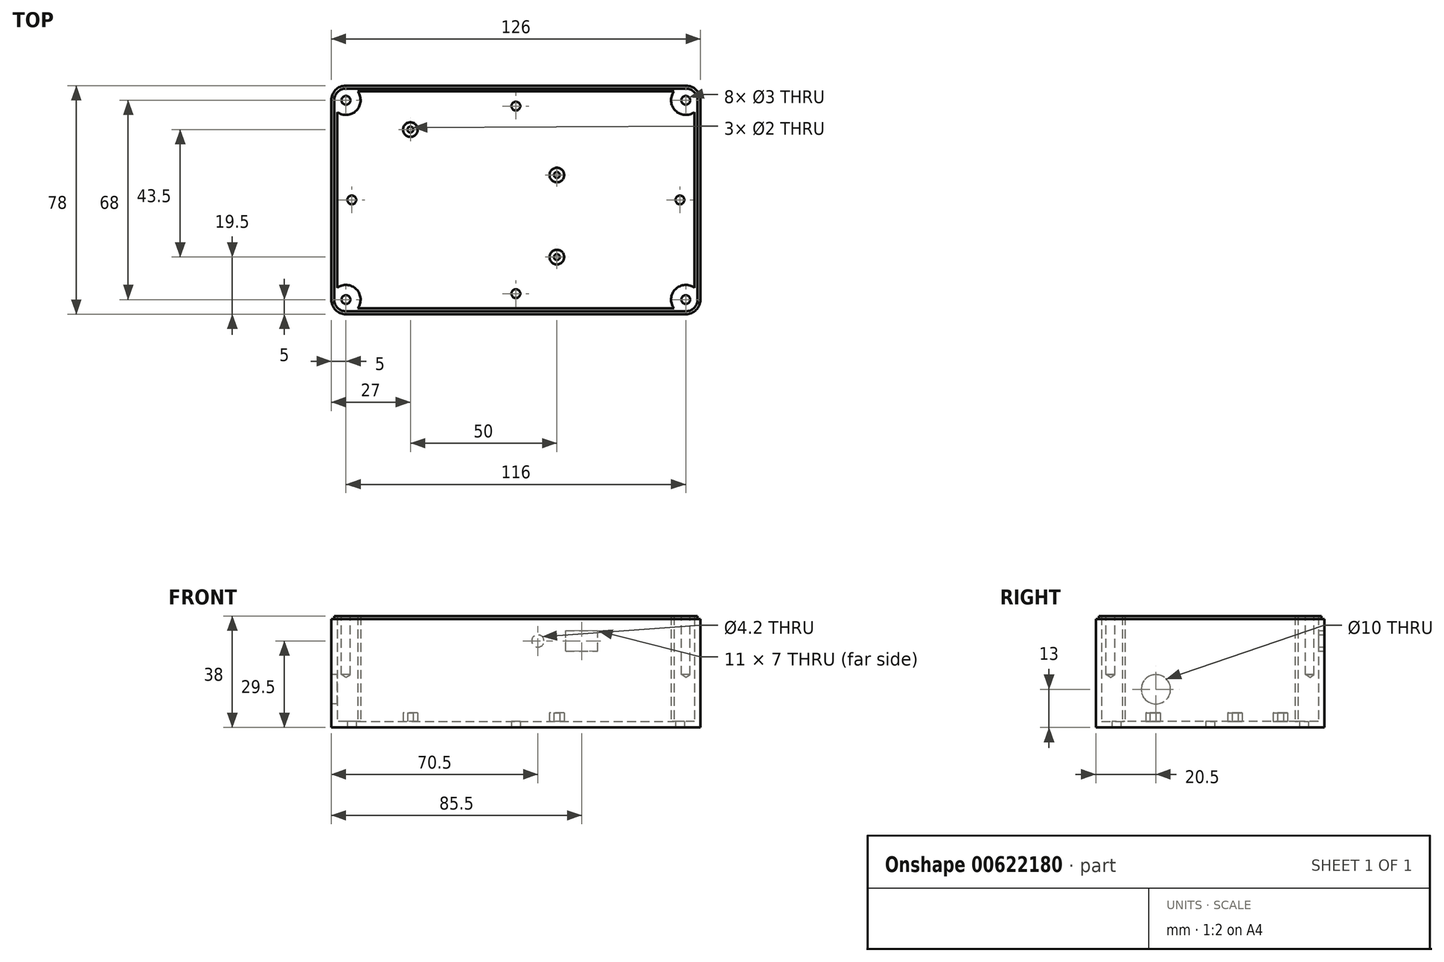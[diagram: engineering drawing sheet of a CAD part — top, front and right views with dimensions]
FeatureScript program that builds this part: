
annotation { "Feature Type Name" : "Feature", "Feature Type Description" : "" }
export const myFeature = defineFeature(function(context is Context, id is Id, definition is map)
    precondition{}
    {
        {
            var Q0;
            Q0=qCreatedBy(makeId("Top.planeOp"),FACE);
            var sketch = newSketch(context, id + "F0", { "sketchPlane" : qUnion([Q0])});
            skLineSegment(sketch, "E0.bottom", {"start": v(51, 27) * mm, "end": v(-51, 27) * mm});
            skLineSegment(sketch, "E0.top", {"start": v(51, -27) * mm, "end": v(-51, -27) * mm});
            skLineSegment(sketch, "E0.left", {"start": v(51, 27) * mm, "end": v(51, -27) * mm});
            skLineSegment(sketch, "E0.right", {"start": v(-51, 27) * mm, "end": v(-51, -27) * mm});
            skPoint(sketch, "E0.middle", {"position": v(0, 0) * mm});
            skPoint(sketch, "E1", {"position": v(-36, 24) * mm});
            skCircle(sketch, "E2", {"center": v(-36, 24) * mm, "radius": 2.5 * mm});
            skLineSegment(sketch, "E3.bottom", {"start": v(-56, 37) * mm, "end": v(56, 37) * mm});
            skLineSegment(sketch, "E3.top", {"start": v(-56, -37) * mm, "end": v(56, -37) * mm});
            skLineSegment(sketch, "E3.left", {"start": v(-61, 32) * mm, "end": v(-61, -32) * mm});
            skLineSegment(sketch, "E3.right", {"start": v(61, 32) * mm, "end": v(61, -32) * mm});
            skPoint(sketch, "E4", {"position": v(14, -19.5) * mm});
            skPoint(sketch, "E5", {"position": v(14, 8.5) * mm});
            skCircle(sketch, "E6", {"center": v(14, 8.5) * mm, "radius": 2.5 * mm});
            skCircle(sketch, "E7", {"center": v(14, -19.5) * mm, "radius": 2.5 * mm});
            skLineSegment(sketch, "E8.bottom", {"start": v(58, 39) * mm, "end": v(-58, 39) * mm});
            skLineSegment(sketch, "E8.top", {"start": v(58, -39) * mm, "end": v(-58, -39) * mm});
            skLineSegment(sketch, "E8.left", {"start": v(63, 34) * mm, "end": v(63, -34) * mm});
            skLineSegment(sketch, "E8.right", {"start": v(-63, 34) * mm, "end": v(-63, -34) * mm});
            skPoint(sketch, "E9.visualSharp", {"position": v(-63, 39) * mm});
            skArc(sketch, "E9.filletArc", {"start": v(-58, 39) * mm, "mid": v(-61.54, 37.54) * mm, "end": v(-63, 34) * mm});
            skPoint(sketch, "E10.visualSharp", {"position": v(63, 39) * mm});
            skArc(sketch, "E10.filletArc", {"start": v(63, 34) * mm, "mid": v(61.54, 37.54) * mm, "end": v(58, 39) * mm});
            skPoint(sketch, "E11.visualSharp", {"position": v(61, 37) * mm});
            skArc(sketch, "E11.filletArc", {"start": v(61, 32) * mm, "mid": v(59.54, 35.54) * mm, "end": v(56, 37) * mm});
            skPoint(sketch, "E12.visualSharp", {"position": v(63, -39) * mm});
            skArc(sketch, "E12.filletArc", {"start": v(58, -39) * mm, "mid": v(61.54, -37.54) * mm, "end": v(63, -34) * mm});
            skPoint(sketch, "E13.visualSharp", {"position": v(61, -37) * mm});
            skArc(sketch, "E13.filletArc", {"start": v(56, -37) * mm, "mid": v(59.54, -35.54) * mm, "end": v(61, -32) * mm});
            skPoint(sketch, "E14.visualSharp", {"position": v(-63, -39) * mm});
            skArc(sketch, "E14.filletArc", {"start": v(-63, -34) * mm, "mid": v(-61.54, -37.54) * mm, "end": v(-58, -39) * mm});
            skPoint(sketch, "E15.visualSharp", {"position": v(-61, -37) * mm});
            skArc(sketch, "E15.filletArc", {"start": v(-61, -32) * mm, "mid": v(-59.54, -35.54) * mm, "end": v(-56, -37) * mm});
            skPoint(sketch, "E16.visualSharp", {"position": v(-61, 37) * mm});
            skArc(sketch, "E16.filletArc", {"start": v(-56, 37) * mm, "mid": v(-59.54, 35.54) * mm, "end": v(-61, 32) * mm});
            skArc(sketch, "E17", {"start": v(-63, 34) * mm, "mid": v(-54.46, 30.46) * mm, "end": v(-58, 39) * mm});
            skArc(sketch, "E18", {"start": v(-58, -39) * mm, "mid": v(-54.46, -30.46) * mm, "end": v(-63, -34) * mm});
            skArc(sketch, "E19", {"start": v(63, -34) * mm, "mid": v(54.46, -30.46) * mm, "end": v(58, -39) * mm});
            skArc(sketch, "E20", {"start": v(58, 39) * mm, "mid": v(54.46, 30.46) * mm, "end": v(63, 34) * mm});
            skPoint(sketch, "E21", {"position": v(0, 32) * mm});
            skPoint(sketch, "E21.positionSnap0", {"position": v(0, 37) * mm});
            skPoint(sketch, "E22", {"position": v(0, -32) * mm});
            skPoint(sketch, "E22.positionSnap0", {"position": v(0, -37) * mm});
            skPoint(sketch, "E23", {"position": v(56, 0) * mm});
            skPoint(sketch, "E23.positionSnap0", {"position": v(61, 0) * mm});
            skPoint(sketch, "E24", {"position": v(-56, 0) * mm});
            skPoint(sketch, "E24.positionSnap0", {"position": v(-61, 0) * mm});
            skSolve(sketch);
        }
        {
            var Q0;
            Q0=makeQuery(id+"F0.imprint","IMPRINT",FACE,{"disambiguationData":[TD([[makeQuery(id+"F0.imprint","IMPRINT",EDGE,{"derivedFrom":sQuery(id+"F0.wireOp",EDGE,"E0.bottom")}),-1.0]])]});
            var Q1;
            Q1=makeQuery(id+"F0.imprint","IMPRINT",FACE,{"disambiguationData":[TD([[makeQuery(id+"F0.imprint","IMPRINT",EDGE,{"derivedFrom":sQuery(id+"F0.wireOp",EDGE,"E0.bottom")}),1.0]])]});
            extrude(context, id + "F1", {"entities" : qUnion([Q0, Q1]), "depth" : 2 * mm, "offsetDistance" : 25 * mm});
        }
        {
            var Q0;
            Q0=makeQuery(id+"F0.imprint","IMPRINT",FACE,{"disambiguationData":[TD([[makeQuery(id+"F0.imprint","IMPRINT",EDGE,{"derivedFrom":sQuery(id+"F0.wireOp",EDGE,"E2")}),1.0]])]});
            var Q1;
            Q1=makeQuery(id+"F0.imprint","IMPRINT",FACE,{"disambiguationData":[TD([[makeQuery(id+"F0.imprint","IMPRINT",EDGE,{"derivedFrom":sQuery(id+"F0.wireOp",EDGE,"E6")}),1.0]])]});
            var Q2;
            Q2=makeQuery(id+"F0.imprint","IMPRINT",FACE,{"disambiguationData":[TD([[makeQuery(id+"F0.imprint","IMPRINT",EDGE,{"derivedFrom":sQuery(id+"F0.wireOp",EDGE,"E7")}),1.0]])]});
            extrude(context, id + "F2", {"entities" : qUnion([Q0, Q1, Q2]), "operationType" : NewBodyOperationType.ADD, "depth" : 5 * mm, "offsetDistance" : 25 * mm});
        }
        {
            var Q0;
            {var subQ0=sQuery(id+"F0.wireOp",EDGE,"E9.filletArc");Q0=makeQuery(id+"F0.imprint","IMPRINT",FACE,{"disambiguationData":[TD([[makeQuery(id+"F0.imprint","IMPRINT",EDGE,{"derivedFrom":subQ0}),1.0]])]});}
            var Q1;
            {var subQ4=sQuery(id+"F0.wireOp",EDGE,"E10.filletArc");Q1=makeQuery(id+"F0.imprint","IMPRINT",FACE,{"disambiguationData":[TD([[makeQuery(id+"F0.imprint","IMPRINT",EDGE,{"derivedFrom":subQ4}),1.0]])]});}
            var Q2;
            {var subQ0=sQuery(id+"F0.wireOp",EDGE,"E11.filletArc");Q2=makeQuery(id+"F0.imprint","IMPRINT",FACE,{"disambiguationData":[TD([[makeQuery(id+"F0.imprint","IMPRINT",EDGE,{"derivedFrom":subQ0}),1.0]])]});}
            var Q3;
            {var subQ0=sQuery(id+"F0.wireOp",EDGE,"E16.filletArc");Q3=makeQuery(id+"F0.imprint","IMPRINT",FACE,{"disambiguationData":[TD([[makeQuery(id+"F0.imprint","IMPRINT",EDGE,{"derivedFrom":subQ0}),1.0]])]});}
            var Q4;
            {var subQ5=sQuery(id+"F0.wireOp",EDGE,"E8.right");Q4=makeQuery(id+"F0.imprint","IMPRINT",FACE,{"disambiguationData":[TD([[makeQuery(id+"F0.imprint","IMPRINT",EDGE,{"derivedFrom":subQ5}),1.0]])]});}
            var Q5;
            {var subQ5=sQuery(id+"F0.wireOp",EDGE,"E8.bottom");Q5=makeQuery(id+"F0.imprint","IMPRINT",FACE,{"disambiguationData":[TD([[makeQuery(id+"F0.imprint","IMPRINT",EDGE,{"derivedFrom":subQ5}),1.0]])]});}
            var Q6;
            {var subQ5=sQuery(id+"F0.wireOp",EDGE,"E8.left");Q6=makeQuery(id+"F0.imprint","IMPRINT",FACE,{"disambiguationData":[TD([[makeQuery(id+"F0.imprint","IMPRINT",EDGE,{"derivedFrom":subQ5}),-1.0]])]});}
            var Q7;
            {var subQ0=sQuery(id+"F0.wireOp",EDGE,"E13.filletArc");Q7=makeQuery(id+"F0.imprint","IMPRINT",FACE,{"disambiguationData":[TD([[makeQuery(id+"F0.imprint","IMPRINT",EDGE,{"derivedFrom":subQ0}),1.0]])]});}
            var Q8;
            {var subQ0=sQuery(id+"F0.wireOp",EDGE,"E15.filletArc");Q8=makeQuery(id+"F0.imprint","IMPRINT",FACE,{"disambiguationData":[TD([[makeQuery(id+"F0.imprint","IMPRINT",EDGE,{"derivedFrom":subQ0}),1.0]])]});}
            var Q9;
            {var subQ1=sQuery(id+"F0.wireOp",EDGE,"E14.filletArc");Q9=makeQuery(id+"F0.imprint","IMPRINT",FACE,{"disambiguationData":[TD([[makeQuery(id+"F0.imprint","IMPRINT",EDGE,{"derivedFrom":subQ1}),1.0]])]});}
            var Q10;
            {var subQ5=sQuery(id+"F0.wireOp",EDGE,"E8.top");Q10=makeQuery(id+"F0.imprint","IMPRINT",FACE,{"disambiguationData":[TD([[makeQuery(id+"F0.imprint","IMPRINT",EDGE,{"derivedFrom":subQ5}),-1.0]])]});}
            var Q11;
            {var subQ4=sQuery(id+"F0.wireOp",EDGE,"E12.filletArc");Q11=makeQuery(id+"F0.imprint","IMPRINT",FACE,{"disambiguationData":[TD([[makeQuery(id+"F0.imprint","IMPRINT",EDGE,{"derivedFrom":subQ4}),1.0]])]});}
            extrude(context, id + "F3", {"entities" : qUnion([Q0, Q1, Q2, Q3, Q4, Q5, Q6, Q7, Q8, Q9, Q10, Q11]), "operationType" : NewBodyOperationType.ADD, "depth" : 38 * mm, "offsetDistance" : 25 * mm});
        }
        {
            var Q0;
            Q0=sQuery(id+"F0.wireOp",VERTEX,"E23");
            var Q1;
            Q1=sQuery(id+"F0.wireOp",VERTEX,"E24");
            var Q2;
            Q2=sQuery(id+"F0.wireOp",VERTEX,"E22");
            var Q3;
            Q3=sQuery(id+"F0.wireOp",VERTEX,"E21");
            var Q4;
            Q4=makeQuery(id+"F1.opExtrude","SWEPT_BODY",BODY,{"disambiguationData":[OSD([sQuery(id+"F0.wireOp",EDGE,"E2"),sQuery(id+"F0.wireOp",EDGE,"E3.bottom"),sQuery(id+"F0.wireOp",EDGE,"E3.top"),sQuery(id+"F0.wireOp",EDGE,"E3.left"),sQuery(id+"F0.wireOp",EDGE,"E3.right"),sQuery(id+"F0.wireOp",EDGE,"E6"),sQuery(id+"F0.wireOp",EDGE,"E7"),sQuery(id+"F0.wireOp",EDGE,"E17"),sQuery(id+"F0.wireOp",EDGE,"E18"),sQuery(id+"F0.wireOp",EDGE,"E19"),sQuery(id+"F0.wireOp",EDGE,"E20")])]});
            hole(context, id + "F4", {"style" : HoleStyle.SIMPLE, "endStyle" : HoleEndStyle.BLIND, "oppositeDirection" : true, "standardTappedOrClearance" : lookupTablePath({ "standard" : "ISO", "size" : "3", "type" : "Drilled" }), "standardBlindInLast" : lookupTablePath({ "standard" : "ISO", "size" : "3", "type" : "Drilled" }), "holeDiameter" : 3 * mm, "majorDiameter" : 5 * mm, "holeDepth" : 5 * mm, "isTappedThrough" : true, "tappedDepth" : 12 * mm, "tapClearance" : 3, "locations" : qUnion([Q0, Q1, Q2, Q3]), "scope" : qUnion([Q4])});
        }
        {
            var Q0;
            Q0=makeQuery(id+"F3.opExtrude","CAP_FACE",FACE,{"disambiguationData":[OSD([sQuery(id+"F0.wireOp",EDGE,"E3.bottom"),sQuery(id+"F0.wireOp",EDGE,"E3.top"),sQuery(id+"F0.wireOp",EDGE,"E3.left"),sQuery(id+"F0.wireOp",EDGE,"E3.right"),sQuery(id+"F0.wireOp",EDGE,"E8.bottom"),sQuery(id+"F0.wireOp",EDGE,"E8.top"),sQuery(id+"F0.wireOp",EDGE,"E8.left"),sQuery(id+"F0.wireOp",EDGE,"E8.right"),sQuery(id+"F0.wireOp",EDGE,"E9.filletArc"),sQuery(id+"F0.wireOp",EDGE,"E10.filletArc"),sQuery(id+"F0.wireOp",EDGE,"E12.filletArc"),sQuery(id+"F0.wireOp",EDGE,"E14.filletArc"),sQuery(id+"F0.wireOp",EDGE,"E17"),sQuery(id+"F0.wireOp",EDGE,"E18"),sQuery(id+"F0.wireOp",EDGE,"E19"),sQuery(id+"F0.wireOp",EDGE,"E20")])],"isStart":false});
            var sketch = newSketch(context, id + "F5", { "sketchPlane" : qUnion([Q0])});
            skArc(sketch, "E25.0", {"start": v(-61, 30) * mm, "mid": v(-54.46, 30.46) * mm, "end": v(-54, 37) * mm});
            skArc(sketch, "E25.1", {"start": v(54, 37) * mm, "mid": v(54.46, 30.46) * mm, "end": v(61, 30) * mm});
            skArc(sketch, "E25.2", {"start": v(61, -30) * mm, "mid": v(54.46, -30.46) * mm, "end": v(54, -37) * mm});
            skArc(sketch, "E25.3", {"start": v(-54, -37) * mm, "mid": v(-54.46, -30.46) * mm, "end": v(-61, -30) * mm});
            skArc(sketch, "E26.0", {"start": v(62, 34) * mm, "mid": v(60.83, 36.83) * mm, "end": v(58, 38) * mm});
            skLineSegment(sketch, "E26.1", {"start": v(62, 34) * mm, "end": v(62, -34) * mm});
            skLineSegment(sketch, "E26.2", {"start": v(58, 38) * mm, "end": v(-58, 38) * mm});
            skArc(sketch, "E26.3", {"start": v(58, -38) * mm, "mid": v(60.83, -36.83) * mm, "end": v(62, -34) * mm});
            skArc(sketch, "E26.4", {"start": v(-58, 38) * mm, "mid": v(-60.83, 36.83) * mm, "end": v(-62, 34) * mm});
            skLineSegment(sketch, "E26.5", {"start": v(-62, 34) * mm, "end": v(-62, -34) * mm});
            skArc(sketch, "E26.6", {"start": v(-62, -34) * mm, "mid": v(-60.83, -36.83) * mm, "end": v(-58, -38) * mm});
            skLineSegment(sketch, "E26.7", {"start": v(58, -38) * mm, "end": v(-58, -38) * mm});
            skSolve(sketch);
        }
        {
            var Q0;
            Q0=sQuery(id+"F5.wireOp",VERTEX,"E25.0.center");
            var Q1;
            Q1=sQuery(id+"F5.wireOp",VERTEX,"E25.1.center");
            var Q2;
            Q2=sQuery(id+"F5.wireOp",VERTEX,"E25.2.center");
            var Q3;
            Q3=sQuery(id+"F5.wireOp",VERTEX,"E25.3.center");
            var Q4;
            Q4=makeQuery(id+"F1.opExtrude","SWEPT_BODY",BODY,{"disambiguationData":[OSD([sQuery(id+"F0.wireOp",EDGE,"E2"),sQuery(id+"F0.wireOp",EDGE,"E3.bottom"),sQuery(id+"F0.wireOp",EDGE,"E3.top"),sQuery(id+"F0.wireOp",EDGE,"E3.left"),sQuery(id+"F0.wireOp",EDGE,"E3.right"),sQuery(id+"F0.wireOp",EDGE,"E6"),sQuery(id+"F0.wireOp",EDGE,"E7"),sQuery(id+"F0.wireOp",EDGE,"E17"),sQuery(id+"F0.wireOp",EDGE,"E18"),sQuery(id+"F0.wireOp",EDGE,"E19"),sQuery(id+"F0.wireOp",EDGE,"E20")])]});
            hole(context, id + "F6", {"style" : HoleStyle.SIMPLE, "endStyle" : HoleEndStyle.BLIND, "standardTappedOrClearance" : lookupTablePath({ "standard" : "ISO", "size" : "3", "type" : "Drilled" }), "standardBlindInLast" : lookupTablePath({ "standard" : "ISO", "size" : "3", "type" : "Drilled" }), "holeDiameter" : 3 * mm, "majorDiameter" : 5 * mm, "holeDepth" : 20 * mm, "isTappedThrough" : true, "tappedDepth" : 12 * mm, "tapClearance" : 3, "locations" : qUnion([Q0, Q1, Q2, Q3]), "scope" : qUnion([Q4])});
        }
        {
            var Q0;
            Q0=makeQuery(id+"F5.imprint","IMPRINT",FACE,{"disambiguationData":[TD([[makeQuery(id+"F5.imprint","IMPRINT",EDGE,{"derivedFrom":sQuery(id+"F5.wireOp",EDGE,"E26.0")}),-1.0]])]});
            extrude(context, id + "F7", {"entities" : qUnion([Q0]), "operationType" : NewBodyOperationType.REMOVE, "oppositeDirection" : true, "depth" : 1 * mm, "offsetDistance" : 25 * mm});
        }
        {
            var Q0;
            Q0=makeQuery(id+"F3.opExtrude","SWEPT_FACE",FACE,{"disambiguationData":[OSD([sQuery(id+"F0.wireOp",EDGE,"E8.right")])]});
            var sketch = newSketch(context, id + "F8", { "sketchPlane" : qUnion([Q0])});
            skLineSegment(sketch, "E27.0", {"start": v(-26.5, 5) * mm, "end": v(-21.5, 5) * mm, "construction": true});
            skPoint(sketch, "E28.0", {"position": v(-27, 0) * mm});
            skPoint(sketch, "E28.1", {"position": v(27, 0) * mm});
            skLineSegment(sketch, "E29", {"start": v(-27, 0) * mm, "end": v(-27, 26.68) * mm, "construction": true});
            skLineSegment(sketch, "E30", {"start": v(27, 0) * mm, "end": v(27, 24.19) * mm, "construction": true});
            skLineSegment(sketch, "E31", {"start": v(27, 13) * mm, "end": v(18.5, 13) * mm, "construction": true});
            skCircle(sketch, "E32", {"center": v(18.5, 13) * mm, "radius": 5 * mm});
            skSolve(sketch);
        }
        {
            var Q0;
            Q0=makeQuery(id+"F8.imprint","IMPRINT",FACE,{"disambiguationData":[TD([[makeQuery(id+"F8.imprint","IMPRINT",EDGE,{"derivedFrom":sQuery(id+"F8.wireOp",EDGE,"E32")}),1.0]])]});
            extrude(context, id + "F9", {"entities" : qUnion([Q0]), "operationType" : NewBodyOperationType.REMOVE, "endBound" : BoundingType.UP_TO_NEXT, "oppositeDirection" : true, "depth" : 25 * mm, "offsetDistance" : 25 * mm});
        }
        {
            var Q0;
            Q0=makeQuery(id+"F3.opExtrude","SWEPT_FACE",FACE,{"disambiguationData":[OSD([sQuery(id+"F0.wireOp",EDGE,"E8.bottom")])]});
            var sketch = newSketch(context, id + "F10", { "sketchPlane" : qUnion([Q0])});
            skLineSegment(sketch, "E33.bottom", {"start": v(-17, 26) * mm, "end": v(-28, 26) * mm});
            skLineSegment(sketch, "E33.top", {"start": v(-17, 33) * mm, "end": v(-28, 33) * mm});
            skLineSegment(sketch, "E33.left", {"start": v(-17, 26) * mm, "end": v(-17, 33) * mm});
            skLineSegment(sketch, "E33.right", {"start": v(-28, 26) * mm, "end": v(-28, 33) * mm});
            skPoint(sketch, "E33.middle", {"position": v(-22.5, 29.5) * mm});
            skCircle(sketch, "E34", {"center": v(-7.5, 29.5) * mm, "radius": 2.1 * mm});
            skSolve(sketch);
        }
        {
            var Q0;
            Q0=makeQuery(id+"F10.imprint","IMPRINT",FACE,{"disambiguationData":[TD([[makeQuery(id+"F10.imprint","IMPRINT",EDGE,{"derivedFrom":sQuery(id+"F10.wireOp",EDGE,"E33.bottom")}),-1.0]])]});
            var Q1;
            Q1=makeQuery(id+"F10.imprint","IMPRINT",FACE,{"disambiguationData":[TD([[makeQuery(id+"F10.imprint","IMPRINT",EDGE,{"derivedFrom":sQuery(id+"F10.wireOp",EDGE,"E34")}),1.0]])]});
            extrude(context, id + "F11", {"entities" : qUnion([Q0, Q1]), "operationType" : NewBodyOperationType.REMOVE, "endBound" : BoundingType.UP_TO_NEXT, "oppositeDirection" : true, "depth" : 25 * mm, "offsetDistance" : 25 * mm});
        }
        {
            var Q0;
            Q0=sQuery(id+"F0.wireOp",VERTEX,"E2.center");
            var Q1;
            Q1=sQuery(id+"F0.wireOp",VERTEX,"E6.center");
            var Q2;
            Q2=sQuery(id+"F0.wireOp",VERTEX,"E4");
            var Q3;
            Q3=makeQuery(id+"F1.opExtrude","SWEPT_BODY",BODY,{"disambiguationData":[OSD([sQuery(id+"F0.wireOp",EDGE,"E2"),sQuery(id+"F0.wireOp",EDGE,"E3.bottom"),sQuery(id+"F0.wireOp",EDGE,"E3.top"),sQuery(id+"F0.wireOp",EDGE,"E3.left"),sQuery(id+"F0.wireOp",EDGE,"E3.right"),sQuery(id+"F0.wireOp",EDGE,"E6"),sQuery(id+"F0.wireOp",EDGE,"E7"),sQuery(id+"F0.wireOp",EDGE,"E17"),sQuery(id+"F0.wireOp",EDGE,"E18"),sQuery(id+"F0.wireOp",EDGE,"E19"),sQuery(id+"F0.wireOp",EDGE,"E20")])]});
            hole(context, id + "F12", {"style" : HoleStyle.SIMPLE, "endStyle" : HoleEndStyle.BLIND, "oppositeDirection" : true, "holeDiameter" : 2 * mm, "majorDiameter" : 5 * mm, "holeDepth" : 5 * mm, "isTappedThrough" : true, "tappedDepth" : 12 * mm, "tapClearance" : 3, "locations" : qUnion([Q0, Q1, Q2]), "scope" : qUnion([Q3])});
        }
    });
